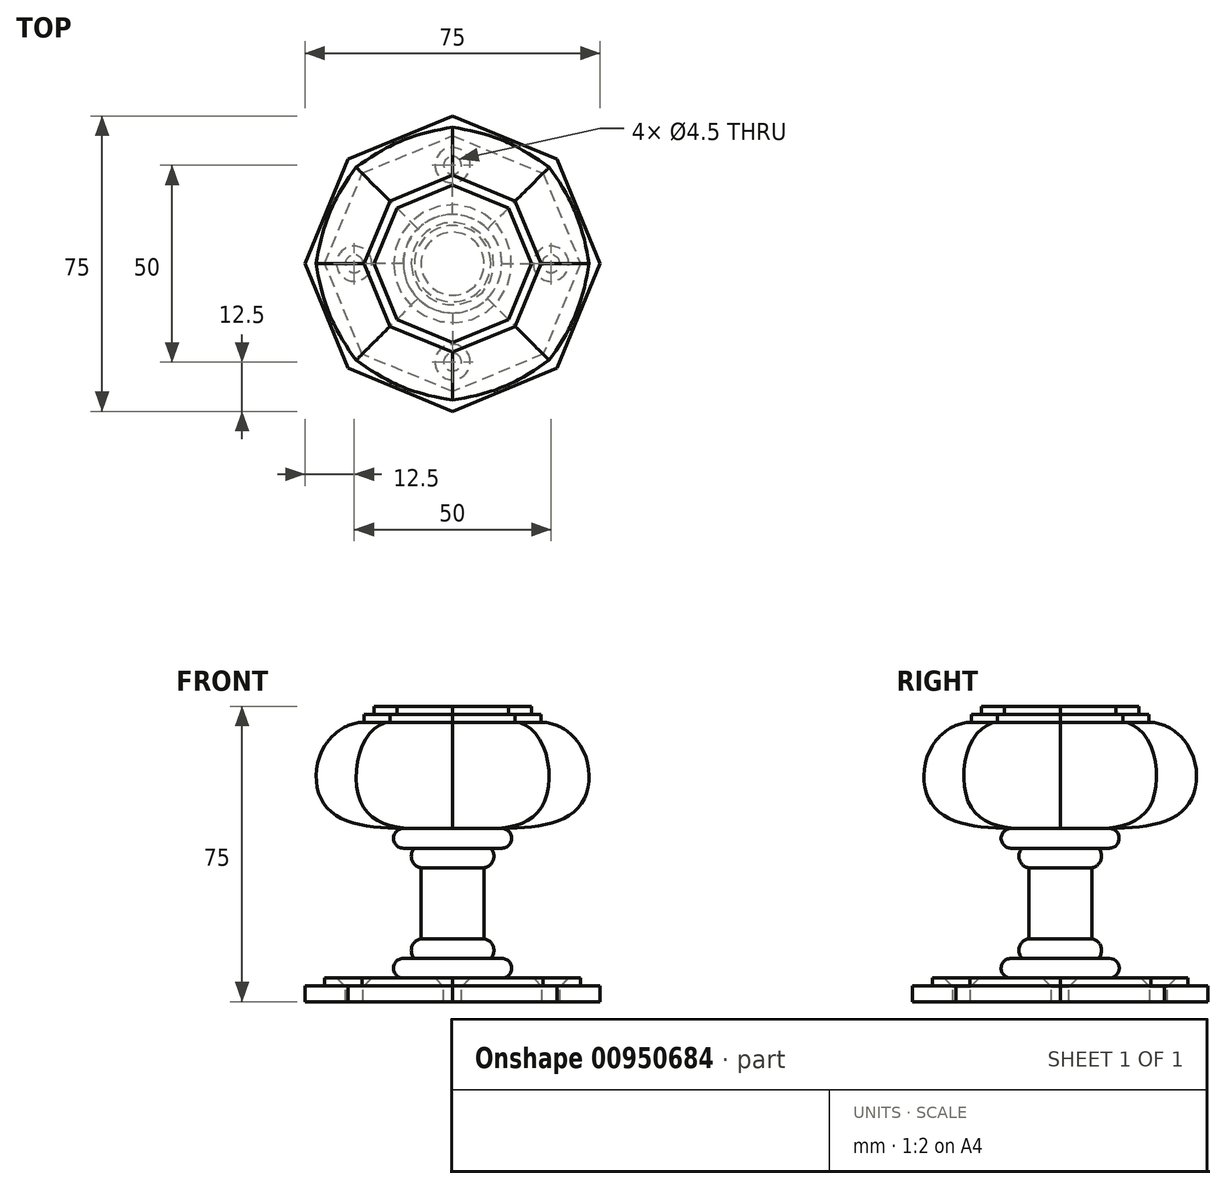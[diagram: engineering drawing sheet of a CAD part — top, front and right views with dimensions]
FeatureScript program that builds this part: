
annotation { "Feature Type Name" : "Feature", "Feature Type Description" : "" }
export const myFeature = defineFeature(function(context is Context, id is Id, definition is map)
    precondition{}
    {
        {
            var Q0;
            Q0=qCreatedBy(makeId("Top.planeOp"),FACE);
            var sketch = newSketch(context, id + "F0", { "sketchPlane" : qUnion([Q0])});
            skCircle(sketch, "E0.cCircle", {"center": v(0, 0) * mm, "radius": 37.5 * mm, "construction": true});
            skLineSegment(sketch, "E0.0", {"start": v(37.5, 0) * mm, "end": v(26.52, -26.52) * mm});
            skLineSegment(sketch, "E0.1", {"start": v(26.52, -26.52) * mm, "end": v(0, -37.5) * mm});
            skLineSegment(sketch, "E0.2", {"start": v(0, -37.5) * mm, "end": v(-26.52, -26.52) * mm});
            skLineSegment(sketch, "E0.3", {"start": v(-26.52, -26.52) * mm, "end": v(-37.5, 0) * mm});
            skLineSegment(sketch, "E0.4", {"start": v(-37.5, 0) * mm, "end": v(-26.52, 26.52) * mm});
            skLineSegment(sketch, "E0.5", {"start": v(-26.52, 26.52) * mm, "end": v(0, 37.5) * mm});
            skLineSegment(sketch, "E0.6", {"start": v(0, 37.5) * mm, "end": v(26.52, 26.52) * mm});
            skLineSegment(sketch, "E0.7", {"start": v(26.52, 26.52) * mm, "end": v(37.5, 0) * mm});
            skSolve(sketch);
        }
        {
            var Q0;
            Q0=makeQuery(id+"F0.imprint","IMPRINT",FACE,{"disambiguationData":[TD([[makeQuery(id+"F0.imprint","IMPRINT",EDGE,{"derivedFrom":sQuery(id+"F0.wireOp",EDGE,"E0.0")}),-1.0]])]});
            extrude(context, id + "F1", {"entities" : qUnion([Q0]), "depth" : 4 * mm, "offsetDistance" : 25 * mm});
        }
        {
            var Q0;
            Q0=makeQuery(id+"F1.opExtrude","CAP_FACE",FACE,{"disambiguationData":[OSD([sQuery(id+"F0.wireOp",EDGE,"E0.0"),sQuery(id+"F0.wireOp",EDGE,"E0.1"),sQuery(id+"F0.wireOp",EDGE,"E0.2"),sQuery(id+"F0.wireOp",EDGE,"E0.3"),sQuery(id+"F0.wireOp",EDGE,"E0.4"),sQuery(id+"F0.wireOp",EDGE,"E0.5"),sQuery(id+"F0.wireOp",EDGE,"E0.6"),sQuery(id+"F0.wireOp",EDGE,"E0.7")])],"isStart":false});
            var sketch = newSketch(context, id + "F2", { "sketchPlane" : qUnion([Q0])});
            skCircle(sketch, "E1.cCircle", {"center": v(0, 0) * mm, "radius": 32.5 * mm, "construction": true});
            skLineSegment(sketch, "E1.0", {"start": v(32.5, 0) * mm, "end": v(22.98, -22.98) * mm});
            skLineSegment(sketch, "E1.1", {"start": v(22.98, -22.98) * mm, "end": v(0, -32.5) * mm});
            skLineSegment(sketch, "E1.2", {"start": v(0, -32.5) * mm, "end": v(-22.98, -22.98) * mm});
            skLineSegment(sketch, "E1.3", {"start": v(-22.98, -22.98) * mm, "end": v(-32.5, 0) * mm});
            skLineSegment(sketch, "E1.4", {"start": v(-32.5, 0) * mm, "end": v(-22.98, 22.98) * mm});
            skLineSegment(sketch, "E1.5", {"start": v(-22.98, 22.98) * mm, "end": v(0, 32.5) * mm});
            skLineSegment(sketch, "E1.6", {"start": v(0, 32.5) * mm, "end": v(22.98, 22.98) * mm});
            skLineSegment(sketch, "E1.7", {"start": v(22.98, 22.98) * mm, "end": v(32.5, 0) * mm});
            skSolve(sketch);
        }
        {
            var Q0;
            Q0=makeQuery(id+"F2.imprint","IMPRINT",FACE,{"disambiguationData":[TD([[makeQuery(id+"F2.imprint","IMPRINT",EDGE,{"derivedFrom":sQuery(id+"F2.wireOp",EDGE,"E1.0")}),-1.0]])]});
            extrude(context, id + "F3", {"entities" : qUnion([Q0]), "operationType" : NewBodyOperationType.ADD, "depth" : 2 * mm, "offsetDistance" : 25 * mm});
        }
        {
            var Q0;
            Q0=qCreatedBy(makeId("Front.planeOp"),FACE);
            var sketch = newSketch(context, id + "F4", { "sketchPlane" : qUnion([Q0])});
            skLineSegment(sketch, "E2", {"start": v(0, 0) * mm, "end": v(0, 93.5) * mm, "construction": true});
            skLineSegment(sketch, "E3", {"start": v(8, 34) * mm, "end": v(8, 16) * mm});
            skLineSegment(sketch, "E4", {"start": v(12.5, 6) * mm, "end": v(0, 6) * mm});
            skLineSegment(sketch, "E5", {"start": v(8, 25) * mm, "end": v(0, 25) * mm, "construction": true});
            skLineSegment(sketch, "E6", {"start": v(0, 6) * mm, "end": v(0, 44) * mm});
            skLineSegment(sketch, "E7", {"start": v(9.7, 11) * mm, "end": v(12.5, 11) * mm});
            skArc(sketch, "E8", {"start": v(12.5, 6) * mm, "mid": v(15, 8.5) * mm, "end": v(12.5, 11) * mm});
            skArc(sketch, "E9", {"start": v(9.7, 11) * mm, "mid": v(10.34, 14) * mm, "end": v(8, 16) * mm});
            skArc(sketch, "E10.MirrorCS", {"start": v(9.7, 39) * mm, "mid": v(10.34, 36) * mm, "end": v(8, 34) * mm});
            skLineSegment(sketch, "E11.MirrorCS", {"start": v(9.7, 39) * mm, "end": v(12.5, 39) * mm});
            skArc(sketch, "E12.MirrorCS", {"start": v(12.5, 44) * mm, "mid": v(15, 41.5) * mm, "end": v(12.5, 39) * mm});
            skLineSegment(sketch, "E13", {"start": v(0, 44) * mm, "end": v(12.5, 44) * mm});
            skSolve(sketch);
        }
        {
            var Q0;
            Q0=makeQuery(id+"F4.imprint","IMPRINT",FACE,{"disambiguationData":[TD([[makeQuery(id+"F4.imprint","IMPRINT",EDGE,{"derivedFrom":sQuery(id+"F4.wireOp",EDGE,"E3")}),-1.0]])]});
            var Q1;
            Q1=sQuery(id+"F4.wireOp",EDGE,"E2");
            revolve(context, id + "F5", {"operationType" : NewBodyOperationType.ADD, "surfaceOperationType" : NewSurfaceOperationType.NEW, "entities" : qUnion([Q0]), "axis" : qUnion([Q1]), "revolveType" : RevolveType.FULL});
        }
        {
            var Q0;
            Q0=makeQuery(id+"F5.opRevolve","SWEPT_FACE",FACE,{"disambiguationData":[OSD([sQuery(id+"F4.wireOp",EDGE,"E13")])]});
            var sketch = newSketch(context, id + "F6", { "sketchPlane" : qUnion([Q0])});
            skCircle(sketch, "E14.0", {"center": v(0, 0) * mm, "radius": 12.5 * mm});
            skSolve(sketch);
        }
        {
            var Q0;
            Q0=makeQuery(id+"F5.opRevolve","SWEPT_FACE",FACE,{"disambiguationData":[OSD([sQuery(id+"F4.wireOp",EDGE,"E13")])]});
            cPlane(context, id + "F7", {"entities" : qUnion([Q0]), "cplaneType" : CPlaneType.OFFSET, "offset" : 6 * mm, "width" : 150 * mm, "height" : 150 * mm});
        }
        {
            var Q0;
            Q0=qCreatedBy(id+"F7.planeOp",FACE);
            var sketch = newSketch(context, id + "F8", { "sketchPlane" : qUnion([Q0])});
            skCircle(sketch, "E15.cCircle", {"center": v(0, 0) * mm, "radius": 32.5 * mm, "construction": true});
            skLineSegment(sketch, "E15.0", {"start": v(32.5, 0) * mm, "end": v(22.98, -22.98) * mm});
            skLineSegment(sketch, "E15.1", {"start": v(22.98, -22.98) * mm, "end": v(0, -32.5) * mm});
            skLineSegment(sketch, "E15.2", {"start": v(0, -32.5) * mm, "end": v(-22.98, -22.98) * mm});
            skLineSegment(sketch, "E15.3", {"start": v(-22.98, -22.98) * mm, "end": v(-32.5, 0) * mm});
            skLineSegment(sketch, "E15.4", {"start": v(-32.5, 0) * mm, "end": v(-22.98, 22.98) * mm});
            skLineSegment(sketch, "E15.5", {"start": v(-22.98, 22.98) * mm, "end": v(0, 32.5) * mm});
            skLineSegment(sketch, "E15.6", {"start": v(0, 32.5) * mm, "end": v(22.98, 22.98) * mm});
            skLineSegment(sketch, "E15.7", {"start": v(22.98, 22.98) * mm, "end": v(32.5, 0) * mm});
            skSolve(sketch);
        }
        {
            var Q0;
            Q0=qCreatedBy(id+"F7.planeOp",FACE);
            cPlane(context, id + "F9", {"entities" : qUnion([Q0]), "cplaneType" : CPlaneType.OFFSET, "offset" : 15 * mm, "width" : 150 * mm, "height" : 150 * mm});
        }
        {
            var Q0;
            Q0=qCreatedBy(id+"F9.planeOp",FACE);
            var sketch = newSketch(context, id + "F10", { "sketchPlane" : qUnion([Q0])});
            skCircle(sketch, "E16.0", {"center": v(0, 0) * mm, "radius": 32.5 * mm});
            skLineSegment(sketch, "E16.1", {"start": v(32.5, 0) * mm, "end": v(22.98, -22.98) * mm});
            skLineSegment(sketch, "E16.2", {"start": v(22.98, -22.98) * mm, "end": v(0, -32.5) * mm});
            skLineSegment(sketch, "E16.3", {"start": v(0, -32.5) * mm, "end": v(-22.98, -22.98) * mm});
            skLineSegment(sketch, "E16.4", {"start": v(-22.98, -22.98) * mm, "end": v(-32.5, 0) * mm});
            skLineSegment(sketch, "E16.5", {"start": v(-32.5, 0) * mm, "end": v(-22.98, 22.98) * mm});
            skLineSegment(sketch, "E16.6", {"start": v(-22.98, 22.98) * mm, "end": v(0, 32.5) * mm});
            skLineSegment(sketch, "E16.7", {"start": v(0, 32.5) * mm, "end": v(22.98, 22.98) * mm});
            skLineSegment(sketch, "E16.8", {"start": v(22.98, 22.98) * mm, "end": v(32.5, 0) * mm});
            skSolve(sketch);
        }
        {
            var Q0;
            Q0=qCreatedBy(id+"F9.planeOp",FACE);
            cPlane(context, id + "F11", {"entities" : qUnion([Q0]), "cplaneType" : CPlaneType.OFFSET, "offset" : 6 * mm, "width" : 150 * mm, "height" : 150 * mm});
        }
        {
            var Q0;
            Q0=qCreatedBy(id+"F11.planeOp",FACE);
            var sketch = newSketch(context, id + "F12", { "sketchPlane" : qUnion([Q0])});
            skCircle(sketch, "E17.cCircle", {"center": v(0, 0) * mm, "radius": 22.5 * mm, "construction": true});
            skLineSegment(sketch, "E17.0", {"start": v(22.5, 0) * mm, "end": v(15.9, -15.9) * mm});
            skLineSegment(sketch, "E17.1", {"start": v(15.9, -15.9) * mm, "end": v(0, -22.5) * mm});
            skLineSegment(sketch, "E17.2", {"start": v(0, -22.5) * mm, "end": v(-15.9, -15.9) * mm});
            skLineSegment(sketch, "E17.3", {"start": v(-15.9, -15.9) * mm, "end": v(-22.5, 0) * mm});
            skLineSegment(sketch, "E17.4", {"start": v(-22.5, 0) * mm, "end": v(-15.9, 15.9) * mm});
            skLineSegment(sketch, "E17.5", {"start": v(-15.9, 15.9) * mm, "end": v(0, 22.5) * mm});
            skLineSegment(sketch, "E17.6", {"start": v(0, 22.5) * mm, "end": v(15.9, 15.9) * mm});
            skLineSegment(sketch, "E17.7", {"start": v(15.9, 15.9) * mm, "end": v(22.5, 0) * mm});
            skSolve(sketch);
        }
        {
            var Q1;
            Q1 = qSketchRegion(id + "F6", true);
            var Q2;
            Q2 = qSketchRegion(id + "F8", true);
            var Q3;
            Q3 = qSketchRegion(id + "F10", true);
            var Q4;
            Q4 = qSketchRegion(id + "F12", true);
            loft(context, id + "F13", {"operationType" : NewBodyOperationType.ADD, "startCondition" : LoftEndDerivativeType.TANGENT_TO_PROFILE, "startMagnitude" : 1, "endCondition" : LoftEndDerivativeType.TANGENT_TO_PROFILE, "endMagnitude" : 1, "sheetProfilesArray" : [{ "sheetProfileEntities" : qUnion([Q1]) }, { "sheetProfileEntities" : qUnion([Q2]) }, { "sheetProfileEntities" : qUnion([Q3]) }, { "sheetProfileEntities" : qUnion([Q4]) }]});
        }
        {
            var Q0;
            Q0=makeQuery(id+"F13.opLoft","CAP_FACE",FACE,{"disambiguationData":[OSD([makeQuery(id+"F12.imprint","IMPRINT",FACE,{"disambiguationData":[TD([[makeQuery(id+"F12.imprint","IMPRINT",EDGE,{"derivedFrom":sQuery(id+"F12.wireOp",EDGE,"E17.0")}),-1.0]])]})])],"isStart":true});
            extrude(context, id + "F14", {"entities" : qUnion([Q0]), "operationType" : NewBodyOperationType.ADD, "depth" : 2 * mm, "offsetDistance" : 25 * mm});
        }
        {
            var Q0;
            Q0=makeQuery(id+"F14.opExtrude","CAP_FACE",FACE,{"disambiguationData":[OSD([makeQuery(id+"F12.imprint","IMPRINT",FACE,{"disambiguationData":[TD([[makeQuery(id+"F12.imprint","IMPRINT",EDGE,{"derivedFrom":sQuery(id+"F12.wireOp",EDGE,"E17.0")}),-1.0]])]})])],"isStart":false});
            var sketch = newSketch(context, id + "F15", { "sketchPlane" : qUnion([Q0])});
            skCircle(sketch, "E18.cCircle", {"center": v(0, 0) * mm, "radius": 20 * mm, "construction": true});
            skLineSegment(sketch, "E18.0", {"start": v(20, 0) * mm, "end": v(14.14, -14.14) * mm});
            skLineSegment(sketch, "E18.1", {"start": v(14.14, -14.14) * mm, "end": v(0, -20) * mm});
            skLineSegment(sketch, "E18.2", {"start": v(0, -20) * mm, "end": v(-14.14, -14.14) * mm});
            skLineSegment(sketch, "E18.3", {"start": v(-14.14, -14.14) * mm, "end": v(-20, 0) * mm});
            skLineSegment(sketch, "E18.4", {"start": v(-20, 0) * mm, "end": v(-14.14, 14.14) * mm});
            skLineSegment(sketch, "E18.5", {"start": v(-14.14, 14.14) * mm, "end": v(0, 20) * mm});
            skLineSegment(sketch, "E18.6", {"start": v(0, 20) * mm, "end": v(14.14, 14.14) * mm});
            skLineSegment(sketch, "E18.7", {"start": v(14.14, 14.14) * mm, "end": v(20, 0) * mm});
            skSolve(sketch);
        }
        {
            var Q0;
            Q0=makeQuery(id+"F15.imprint","IMPRINT",FACE,{"disambiguationData":[TD([[makeQuery(id+"F15.imprint","IMPRINT",EDGE,{"derivedFrom":sQuery(id+"F15.wireOp",EDGE,"E18.0")}),-1.0]])]});
            extrude(context, id + "F16", {"entities" : qUnion([Q0]), "operationType" : NewBodyOperationType.ADD, "depth" : 2 * mm, "offsetDistance" : 25 * mm});
        }
        {
            var Q0;
            Q0=makeQuery(id+"F3.opExtrude","CAP_FACE",FACE,{"disambiguationData":[OSD([sQuery(id+"F2.wireOp",EDGE,"E1.0"),sQuery(id+"F2.wireOp",EDGE,"E1.1"),sQuery(id+"F2.wireOp",EDGE,"E1.2"),sQuery(id+"F2.wireOp",EDGE,"E1.3"),sQuery(id+"F2.wireOp",EDGE,"E1.4"),sQuery(id+"F2.wireOp",EDGE,"E1.5"),sQuery(id+"F2.wireOp",EDGE,"E1.6"),sQuery(id+"F2.wireOp",EDGE,"E1.7")])],"isStart":false});
            var sketch = newSketch(context, id + "F17", { "sketchPlane" : qUnion([Q0])});
            skPoint(sketch, "E19", {"position": v(-25, 0) * mm});
            skCircle(sketch, "E20", {"center": v(0, 0) * mm, "radius": 25 * mm, "construction": true});
            skPoint(sketch, "E21", {"position": v(25, 0) * mm});
            skPoint(sketch, "E22", {"position": v(0, 25) * mm});
            skPoint(sketch, "E23", {"position": v(0, -25) * mm});
            skSolve(sketch);
        }
        {
            var Q0;
            Q0=sQuery(id+"F17.wireOp",VERTEX,"E19");
            var Q1;
            Q1=sQuery(id+"F17.wireOp",VERTEX,"E23");
            var Q2;
            Q2=sQuery(id+"F17.wireOp",VERTEX,"E21");
            var Q3;
            Q3=sQuery(id+"F17.wireOp",VERTEX,"E22");
            var Q4;
            Q4=makeQuery(id+"F1.opExtrude","SWEPT_BODY",BODY,{"disambiguationData":[OSD([sQuery(id+"F0.wireOp",EDGE,"E0.0"),sQuery(id+"F0.wireOp",EDGE,"E0.1"),sQuery(id+"F0.wireOp",EDGE,"E0.2"),sQuery(id+"F0.wireOp",EDGE,"E0.3"),sQuery(id+"F0.wireOp",EDGE,"E0.4"),sQuery(id+"F0.wireOp",EDGE,"E0.5"),sQuery(id+"F0.wireOp",EDGE,"E0.6"),sQuery(id+"F0.wireOp",EDGE,"E0.7")])]});
            hole(context, id + "F18", {"style" : HoleStyle.C_SINK, "endStyle" : HoleEndStyle.BLIND, "standardTappedOrClearance" : lookupTablePath({ "fit" : "Normal", "standard" : "ISO", "size" : "M4", "type" : "Clearance" }), "standardBlindInLast" : lookupTablePath({ "fit" : "Normal", "standard" : "ISO", "engagement" : "75%", "pitch" : "0.7 mm", "size" : "M4", "type" : "Clearance & tapped" }), "holeDiameter" : 4.5 * mm, "cSinkDiameter" : 8.96 * mm, "cSinkAngle" : 90 * degree, "majorDiameter" : 4 * mm, "holeDepth" : 8 * mm, "isTappedThrough" : true, "tappedDepth" : 5.9 * mm, "tapClearance" : 3, "locations" : qUnion([Q0, Q1, Q2, Q3]), "scope" : qUnion([Q4])});
        }
    });
